# Revit family: Magnuson-Pictor-Showcase
name_source: partatom
category: Furniture
revit_build: Autodesk Revit 2014 (Build: 20130308_1515(x64)
units: mm (PartAtom-declared; Revit-internal decimal feet)

## types (5) — shared parameters
# of Shelf = 4
Assembly Code = E2020200
Bottom Finish = MAG - Aluminum
Chasis Finish = MAG - Glass
Frame Finish = MAG - Powdercoat White
Glides Finish = MAG - Plastic Black
Handle Finish = MAG - Powdercoat White
Height = 71 11/16"
Keynote = 12500
Light Finish = MAG - Plastic Black
Low Emitting Finish = Yes
Low Emitting Material = Yes
Manufacturer = MAGNUSON GROUP
Salvage or Reuse = Yes
Shelf Array Dist = 13 19/32"
Shelf Finish = MAG - Glass
Top Finish = MAG - Aluminum
Type Comments = PICTOR SHOWCASES
URL = https://magnusongroup.com
zero-valued in all types: Percentage of Recycled Content

## per-type parameters (varying)
| type | Back Handle | Depth | Description | Light Array Dist | Light Dist | Shelf Depth | Width |
| VA040 | No | 15 3/4" | 15"W X 15"D Showcase | 0" | 7 7/8" | 14 1/2" | 15 3/4" |
| VA050 | No | 19 11/16" | 15"W X 20"D Showcase | 0" | 9 27/32" | 18 7/16" | 19 11/16" |
| VA060 | No | 23 5/8" | 15"W X 31"D Showcase | 11 13/16" | 5 29/32" | 22 3/8" | 15 3/4" |
| VA080 | Yes | 31 1/2" | 15"W X 31"D Showcase | 15 3/4" | 7 7/8" | 30 1/4" | 15 3/4" |
| VA0100 | Yes | 39 3/8" | 15"W X 40"D Showcase | 19 11/16" | 9 27/32" | 38 1/8" | 15 3/4" |

note: column(s) folded — value = type name in every type: Model

## geometry (parser evidence)
native form markers: Sweep x1
no freeform markers — native parametric forms only
